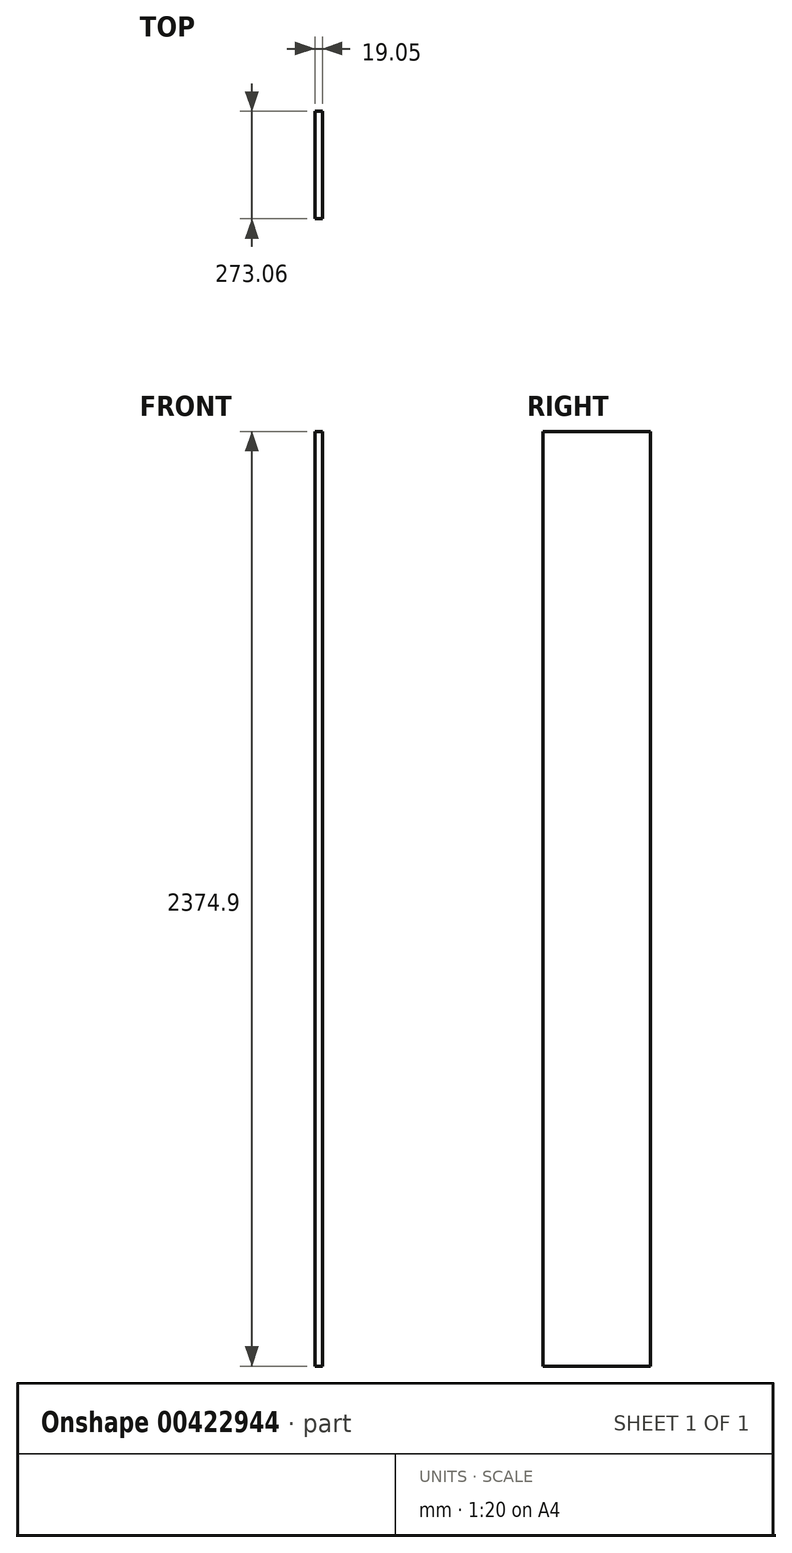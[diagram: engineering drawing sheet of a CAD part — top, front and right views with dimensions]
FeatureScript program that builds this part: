
annotation { "Feature Type Name" : "Feature", "Feature Type Description" : "" }
export const myFeature = defineFeature(function(context is Context, id is Id, definition is map)
    precondition{}
    {
        {
            var Q0;
            Q0=qCreatedBy(makeId("Right.planeOp"),FACE);
            var sketch = newSketch(context, id + "F0", { "sketchPlane" : qUnion([Q0])});
            skLineSegment(sketch, "E0.bottom", {"start": v(136.53, 1187.45) * mm, "end": v(-136.52, 1187.45) * mm});
            skLineSegment(sketch, "E0.top", {"start": v(136.52, -1187.45) * mm, "end": v(-136.53, -1187.45) * mm});
            skLineSegment(sketch, "E0.left", {"start": v(136.53, 1187.45) * mm, "end": v(136.52, -1187.45) * mm});
            skLineSegment(sketch, "E0.right", {"start": v(-136.52, 1187.45) * mm, "end": v(-136.53, -1187.45) * mm});
            skPoint(sketch, "E0.middle", {"position": v(0, 0) * mm});
            skSolve(sketch);
        }
        {
            var Q0;
            Q0 = qSketchRegion(id + "F0", true);
            extrude(context, id + "F1", {"entities" : qUnion([Q0]), "depth" : 19.05 * mm, "offsetDistance" : 25.4 * mm});
        }
    });
